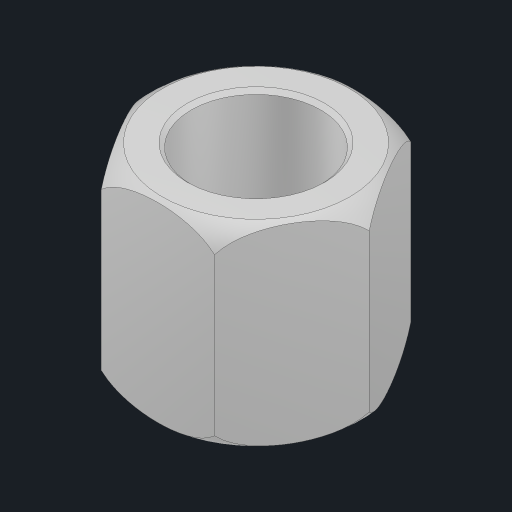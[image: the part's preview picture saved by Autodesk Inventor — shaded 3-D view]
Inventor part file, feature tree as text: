
AUTODESK INVENTOR PART (.ipt)
format: ipt  version: 2023 (Build 270158000, 158)  size: 208,896 bytes
history: native  units: in
note: dims shown in document units (in); Inventor stores cm internally (conversion verified against a paired STEP export)
features: other x13, sketch x6, chamfer x3, hole x3, extrude x2
ambient origin geometry x8: Origin, YZ Plane, XZ Plane, XY Plane, X Axis, Y Axis, Z Axis, Center Point
bodies: Solid1 (feature_tree), Body (feature_tree)
feature tree (27):
  other  "Table"
  other  "Standoff .25"
  other  "Standoff .50"
  other  "Standoff .75"
  other  "Standoff .875"
  other  "Standoff 1.00"
  other  "Standoff 1.50"
  other  "Standoff 2.00"
  other  "Standoff 2.50"
  other  "Standoff 3.00"
  other  "Standoff 4.00"
  other  "Standoff 5.00"
  other  "Standoff 6.00"
  extrude  "Hole 2"  TaperAngle=0.0deg  [1 undecoded]
  extrude  "Hole 1"  Depth=0.5in TaperAngle=0.0deg
  chamfer  "Hole 2 Chamfer 1"  Distance=0.5in
  chamfer  "Hole 1 Chamfer 1"  Distance=0.005in Angle=45.0deg
  hole  "Hole 2 Chamfer 2"  [1 undecoded]
  hole  "Hole 1 Chamfer 2"  [1 undecoded]
  chamfer  "Hole 2 Chamfer 1 For Short"  Distance=0.1195in
  hole  "Hole 2 Chamfer 2 For Short"  [1 undecoded]
  sketch  "Sketch1"  dims[d0=0.25in d2=0.0in]
  sketch  "Sketch2"  dims[d3=0.165in d4=0.5in d5=0.0in]
  sketch  "Sketch3"  dims[d6=0.165in d7=0.5in d8=0.0in d9=0.005in d10=0.0049in d11=45.0deg]
  sketch  "Sketch4"  dims[d12=0.005in d13=0.0049in d14=45.0deg d15=0.1195in]
  sketch  "Sketch5"  dims[d16=0.065in d17=0.025in]
  sketch  "Sketch7"  dims[d18=90.0deg d19=0.1195in d20=0.065in d21=0.025in d22=90.0deg d30=0.005in d31=0.0049in d32=45.0deg d33=0.1195in d34=0.065in d35=0.025in d36=90.0deg]
note: 4 required parameter values undecoded (feature->parameter linkage not recoverable at this tier; creation-order binding heuristic only, values carry confidence <= 0.55)
